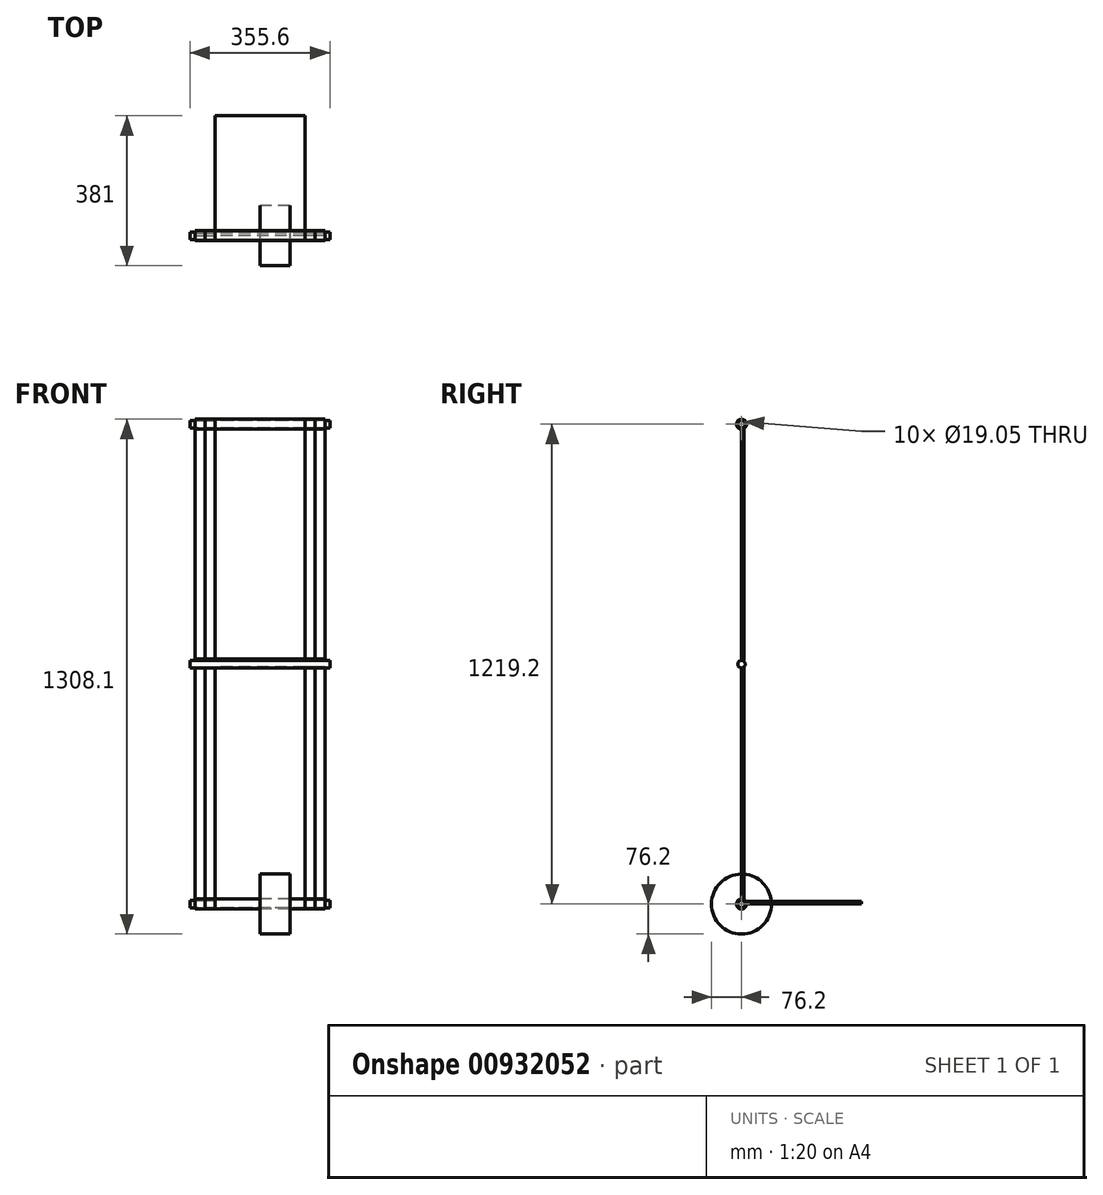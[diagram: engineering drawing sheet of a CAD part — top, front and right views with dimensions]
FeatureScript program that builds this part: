
annotation { "Feature Type Name" : "Feature", "Feature Type Description" : "" }
export const myFeature = defineFeature(function(context is Context, id is Id, definition is map)
    precondition{}
    {
        {
            var Q0;
            Q0=qCreatedBy(makeId("Right.planeOp"),FACE);
            var sketch = newSketch(context, id + "F0", { "sketchPlane" : qUnion([Q0])});
            skLineSegment(sketch, "E0", {"start": v(0, 0) * mm, "end": v(0, 1219.2) * mm});
            skLineSegment(sketch, "E1", {"start": v(0, 0) * mm, "end": v(304.8, 0) * mm});
            skLineSegment(sketch, "E2.0", {"start": v(6.35, 6.35) * mm, "end": v(6.35, 1219.2) * mm});
            skLineSegment(sketch, "E3.0", {"start": v(6.35, 6.35) * mm, "end": v(304.8, 6.35) * mm});
            skLineSegment(sketch, "E4", {"start": v(304.8, 6.35) * mm, "end": v(304.8, 0) * mm});
            skLineSegment(sketch, "E5", {"start": v(0, 1219.2) * mm, "end": v(6.35, 1219.2) * mm});
            skCircle(sketch, "E6", {"center": v(0, 0) * mm, "radius": 12.7 * mm});
            skCircle(sketch, "E7", {"center": v(0, 609.6) * mm, "radius": 12.7 * mm});
            skCircle(sketch, "E8", {"center": v(0, 1219.2) * mm, "radius": 12.7 * mm});
            skCircle(sketch, "E9", {"center": v(0, 609.6) * mm, "radius": 9.53 * mm});
            skCircle(sketch, "E10", {"center": v(0, 1219.2) * mm, "radius": 9.53 * mm});
            skCircle(sketch, "E11", {"center": v(0, 0) * mm, "radius": 9.53 * mm});
            skSolve(sketch);
        }
        {
            var Q0;
            {var subQ0=sQuery(id+"F0.wireOp",EDGE,"E7");var subQ1=sQuery(id+"F0.wireOp",EDGE,"E0");var subQ2=makeQuery(id+"F0.imprint","INTERSECT",VERTEX,{"disambiguationData":[OD(0.0)],"derivedFrom":[subQ1,subQ0]});Q0=makeQuery(id+"F0.imprint","IMPRINT",FACE,{"disambiguationData":[TD([[makeQuery(id+"F0.imprint","IMPRINT",EDGE,{"disambiguationData":[TD([[subQ2,-1.0]])],"derivedFrom":subQ1}),1.0]])]});}
            var Q1;
            {var subQ0=sQuery(id+"F0.wireOp",EDGE,"E4");Q1=makeQuery(id+"F0.imprint","IMPRINT",FACE,{"disambiguationData":[TD([[makeQuery(id+"F0.imprint","IMPRINT",EDGE,{"derivedFrom":subQ0}),-1.0]])]});}
            var Q2;
            {var subQ0=sQuery(id+"F0.wireOp",EDGE,"E7");var subQ1=sQuery(id+"F0.wireOp",EDGE,"E2.0");var subQ2=makeQuery(id+"F0.imprint","INTERSECT",VERTEX,{"disambiguationData":[OD(0.0)],"derivedFrom":[subQ1,subQ0]});Q2=makeQuery(id+"F0.imprint","IMPRINT",FACE,{"disambiguationData":[TD([[makeQuery(id+"F0.imprint","IMPRINT",EDGE,{"disambiguationData":[TD([[subQ2,-1.0]])],"derivedFrom":subQ1}),-1.0]])]});}
            var Q3;
            {var subQ0=sQuery(id+"F0.wireOp",EDGE,"E8");var subQ1=sQuery(id+"F0.wireOp",EDGE,"E0");var subQ2=makeQuery(id+"F0.imprint","INTERSECT",VERTEX,{"derivedFrom":[subQ1,subQ0]});Q3=makeQuery(id+"F0.imprint","IMPRINT",FACE,{"disambiguationData":[TD([[makeQuery(id+"F0.imprint","IMPRINT",EDGE,{"disambiguationData":[TD([[subQ2,-1.0]])],"derivedFrom":subQ1}),1.0]])]});}
            var Q4;
            {var subQ0=sQuery(id+"F0.wireOp",EDGE,"E7");var subQ1=sQuery(id+"F0.wireOp",EDGE,"E0");var subQ2=makeQuery(id+"F0.imprint","INTERSECT",VERTEX,{"disambiguationData":[OD(0.0)],"derivedFrom":[subQ1,subQ0]});Q4=makeQuery(id+"F0.imprint","IMPRINT",FACE,{"disambiguationData":[TD([[makeQuery(id+"F0.imprint","IMPRINT",EDGE,{"disambiguationData":[TD([[subQ2,-1.0]])],"derivedFrom":subQ1}),-1.0]])]});}
            var Q5;
            {var subQ0=sQuery(id+"F0.wireOp",EDGE,"E6");var subQ1=sQuery(id+"F0.wireOp",EDGE,"E0");var subQ2=makeQuery(id+"F0.imprint","INTERSECT",VERTEX,{"derivedFrom":[subQ1,subQ0]});Q5=makeQuery(id+"F0.imprint","IMPRINT",FACE,{"disambiguationData":[TD([[makeQuery(id+"F0.imprint","IMPRINT",EDGE,{"disambiguationData":[TD([[subQ2,-1.0]])],"derivedFrom":subQ1}),-1.0]])]});}
            var Q6;
            {var subQ0=sQuery(id+"F0.wireOp",EDGE,"E8");var subQ1=sQuery(id+"F0.wireOp",EDGE,"E0");var subQ2=makeQuery(id+"F0.imprint","INTERSECT",VERTEX,{"derivedFrom":[subQ1,subQ0]});Q6=makeQuery(id+"F0.imprint","IMPRINT",FACE,{"disambiguationData":[TD([[makeQuery(id+"F0.imprint","IMPRINT",EDGE,{"disambiguationData":[TD([[subQ2,-1.0]])],"derivedFrom":subQ1}),-1.0]])]});}
            var Q7;
            {var subQ0=sQuery(id+"F0.wireOp",EDGE,"E7");var subQ1=sQuery(id+"F0.wireOp",EDGE,"E0");var subQ2=makeQuery(id+"F0.imprint","INTERSECT",VERTEX,{"disambiguationData":[OD(1.0)],"derivedFrom":[subQ1,subQ0]});Q7=makeQuery(id+"F0.imprint","IMPRINT",FACE,{"disambiguationData":[TD([[makeQuery(id+"F0.imprint","IMPRINT",EDGE,{"disambiguationData":[TD([[subQ2,-1.0]])],"derivedFrom":subQ1}),-1.0]])]});}
            var Q8;
            {var subQ0=sQuery(id+"F0.wireOp",EDGE,"E7");var subQ1=sQuery(id+"F0.wireOp",EDGE,"E0");var subQ2=makeQuery(id+"F0.imprint","INTERSECT",VERTEX,{"disambiguationData":[OD(1.0)],"derivedFrom":[subQ1,subQ0]});Q8=makeQuery(id+"F0.imprint","IMPRINT",FACE,{"disambiguationData":[TD([[makeQuery(id+"F0.imprint","IMPRINT",EDGE,{"disambiguationData":[TD([[subQ2,1.0]])],"derivedFrom":subQ1}),-1.0]])]});}
            var Q9;
            {var subQ0=sQuery(id+"F0.wireOp",EDGE,"E6");var subQ1=sQuery(id+"F0.wireOp",EDGE,"E0");var subQ2=makeQuery(id+"F0.imprint","INTERSECT",VERTEX,{"derivedFrom":[subQ1,subQ0]});Q9=makeQuery(id+"F0.imprint","IMPRINT",FACE,{"disambiguationData":[TD([[makeQuery(id+"F0.imprint","IMPRINT",EDGE,{"disambiguationData":[TD([[subQ2,1.0]])],"derivedFrom":subQ1}),-1.0]])]});}
            var Q10;
            {var subQ0=sQuery(id+"F0.wireOp",EDGE,"E6");var subQ1=sQuery(id+"F0.wireOp",EDGE,"E2.0");var subQ2=makeQuery(id+"F0.imprint","INTERSECT",VERTEX,{"derivedFrom":[subQ1,subQ0]});Q10=makeQuery(id+"F0.imprint","IMPRINT",FACE,{"disambiguationData":[TD([[makeQuery(id+"F0.imprint","IMPRINT",EDGE,{"disambiguationData":[TD([[subQ2,1.0]])],"derivedFrom":subQ1}),-1.0]])]});}
            var Q11;
            {var subQ0=sQuery(id+"F0.wireOp",EDGE,"E6");var subQ1=sQuery(id+"F0.wireOp",EDGE,"E1");var subQ2=makeQuery(id+"F0.imprint","INTERSECT",VERTEX,{"derivedFrom":[subQ1,subQ0]});Q11=makeQuery(id+"F0.imprint","IMPRINT",FACE,{"disambiguationData":[TD([[makeQuery(id+"F0.imprint","IMPRINT",EDGE,{"disambiguationData":[TD([[subQ2,1.0]])],"derivedFrom":subQ1}),1.0]])]});}
            var Q12;
            {var subQ0=sQuery(id+"F0.wireOp",EDGE,"E6");var subQ1=sQuery(id+"F0.wireOp",EDGE,"E0");var subQ2=makeQuery(id+"F0.imprint","INTERSECT",VERTEX,{"derivedFrom":[subQ1,subQ0]});Q12=makeQuery(id+"F0.imprint","IMPRINT",FACE,{"disambiguationData":[TD([[makeQuery(id+"F0.imprint","IMPRINT",EDGE,{"disambiguationData":[TD([[subQ2,1.0]])],"derivedFrom":subQ1}),1.0]])]});}
            extrude(context, id + "F1", {"entities" : qUnion([Q0, Q1, Q2, Q3, Q4, Q5, Q6, Q7, Q8, Q9, Q10, Q11, Q12]), "endBound" : BoundingType.SYMMETRIC, "depth" : 228.6 * mm, "offsetDistance" : 25.4 * mm});
        }
        {
            var Q0;
            {var subQ0=sQuery(id+"F0.wireOp",EDGE,"E7");var subQ1=sQuery(id+"F0.wireOp",EDGE,"E0");var subQ2=makeQuery(id+"F0.imprint","INTERSECT",VERTEX,{"disambiguationData":[OD(0.0)],"derivedFrom":[subQ1,subQ0]});Q0=makeQuery(id+"F0.imprint","IMPRINT",FACE,{"disambiguationData":[TD([[makeQuery(id+"F0.imprint","IMPRINT",EDGE,{"disambiguationData":[TD([[subQ2,-1.0]])],"derivedFrom":subQ1}),1.0]])]});}
            var Q1;
            {var subQ0=sQuery(id+"F0.wireOp",EDGE,"E6");var subQ1=sQuery(id+"F0.wireOp",EDGE,"E2.0");var subQ2=makeQuery(id+"F0.imprint","INTERSECT",VERTEX,{"derivedFrom":[subQ1,subQ0]});Q1=makeQuery(id+"F0.imprint","IMPRINT",FACE,{"disambiguationData":[TD([[makeQuery(id+"F0.imprint","IMPRINT",EDGE,{"disambiguationData":[TD([[subQ2,1.0]])],"derivedFrom":subQ1}),-1.0]])]});}
            var Q2;
            {var subQ0=sQuery(id+"F0.wireOp",EDGE,"E7");var subQ1=sQuery(id+"F0.wireOp",EDGE,"E2.0");var subQ2=makeQuery(id+"F0.imprint","INTERSECT",VERTEX,{"disambiguationData":[OD(0.0)],"derivedFrom":[subQ1,subQ0]});Q2=makeQuery(id+"F0.imprint","IMPRINT",FACE,{"disambiguationData":[TD([[makeQuery(id+"F0.imprint","IMPRINT",EDGE,{"disambiguationData":[TD([[subQ2,-1.0]])],"derivedFrom":subQ1}),-1.0]])]});}
            var Q3;
            {var subQ0=sQuery(id+"F0.wireOp",EDGE,"E8");var subQ1=sQuery(id+"F0.wireOp",EDGE,"E0");var subQ2=makeQuery(id+"F0.imprint","INTERSECT",VERTEX,{"derivedFrom":[subQ1,subQ0]});Q3=makeQuery(id+"F0.imprint","IMPRINT",FACE,{"disambiguationData":[TD([[makeQuery(id+"F0.imprint","IMPRINT",EDGE,{"disambiguationData":[TD([[subQ2,-1.0]])],"derivedFrom":subQ1}),1.0]])]});}
            var Q4;
            {var subQ0=sQuery(id+"F0.wireOp",EDGE,"E7");var subQ1=sQuery(id+"F0.wireOp",EDGE,"E0");var subQ2=makeQuery(id+"F0.imprint","INTERSECT",VERTEX,{"disambiguationData":[OD(1.0)],"derivedFrom":[subQ1,subQ0]});Q4=makeQuery(id+"F0.imprint","IMPRINT",FACE,{"disambiguationData":[TD([[makeQuery(id+"F0.imprint","IMPRINT",EDGE,{"disambiguationData":[TD([[subQ2,1.0]])],"derivedFrom":subQ1}),-1.0]])]});}
            var Q5;
            {var subQ0=sQuery(id+"F0.wireOp",EDGE,"E7");var subQ1=sQuery(id+"F0.wireOp",EDGE,"E0");var subQ2=makeQuery(id+"F0.imprint","INTERSECT",VERTEX,{"disambiguationData":[OD(0.0)],"derivedFrom":[subQ1,subQ0]});Q5=makeQuery(id+"F0.imprint","IMPRINT",FACE,{"disambiguationData":[TD([[makeQuery(id+"F0.imprint","IMPRINT",EDGE,{"disambiguationData":[TD([[subQ2,-1.0]])],"derivedFrom":subQ1}),-1.0]])]});}
            var Q6;
            {var subQ0=sQuery(id+"F0.wireOp",EDGE,"E6");var subQ1=sQuery(id+"F0.wireOp",EDGE,"E0");var subQ2=makeQuery(id+"F0.imprint","INTERSECT",VERTEX,{"derivedFrom":[subQ1,subQ0]});Q6=makeQuery(id+"F0.imprint","IMPRINT",FACE,{"disambiguationData":[TD([[makeQuery(id+"F0.imprint","IMPRINT",EDGE,{"disambiguationData":[TD([[subQ2,1.0]])],"derivedFrom":subQ1}),1.0]])]});}
            var Q7;
            {var subQ0=sQuery(id+"F0.wireOp",EDGE,"E6");var subQ1=sQuery(id+"F0.wireOp",EDGE,"E0");var subQ2=makeQuery(id+"F0.imprint","INTERSECT",VERTEX,{"derivedFrom":[subQ1,subQ0]});Q7=makeQuery(id+"F0.imprint","IMPRINT",FACE,{"disambiguationData":[TD([[makeQuery(id+"F0.imprint","IMPRINT",EDGE,{"disambiguationData":[TD([[subQ2,-1.0]])],"derivedFrom":subQ1}),-1.0]])]});}
            var Q8;
            {var subQ0=sQuery(id+"F0.wireOp",EDGE,"E7");var subQ1=sQuery(id+"F0.wireOp",EDGE,"E0");var subQ2=makeQuery(id+"F0.imprint","INTERSECT",VERTEX,{"disambiguationData":[OD(1.0)],"derivedFrom":[subQ1,subQ0]});Q8=makeQuery(id+"F0.imprint","IMPRINT",FACE,{"disambiguationData":[TD([[makeQuery(id+"F0.imprint","IMPRINT",EDGE,{"disambiguationData":[TD([[subQ2,-1.0]])],"derivedFrom":subQ1}),-1.0]])]});}
            var Q9;
            {var subQ0=sQuery(id+"F0.wireOp",EDGE,"E6");var subQ1=sQuery(id+"F0.wireOp",EDGE,"E0");var subQ2=makeQuery(id+"F0.imprint","INTERSECT",VERTEX,{"derivedFrom":[subQ1,subQ0]});Q9=makeQuery(id+"F0.imprint","IMPRINT",FACE,{"disambiguationData":[TD([[makeQuery(id+"F0.imprint","IMPRINT",EDGE,{"disambiguationData":[TD([[subQ2,1.0]])],"derivedFrom":subQ1}),-1.0]])]});}
            var Q10;
            {var subQ0=sQuery(id+"F0.wireOp",EDGE,"E8");var subQ1=sQuery(id+"F0.wireOp",EDGE,"E0");var subQ2=makeQuery(id+"F0.imprint","INTERSECT",VERTEX,{"derivedFrom":[subQ1,subQ0]});Q10=makeQuery(id+"F0.imprint","IMPRINT",FACE,{"disambiguationData":[TD([[makeQuery(id+"F0.imprint","IMPRINT",EDGE,{"disambiguationData":[TD([[subQ2,-1.0]])],"derivedFrom":subQ1}),-1.0]])]});}
            var Q11;
            {var subQ0=sQuery(id+"F0.wireOp",EDGE,"E6");var subQ1=sQuery(id+"F0.wireOp",EDGE,"E1");var subQ2=makeQuery(id+"F0.imprint","INTERSECT",VERTEX,{"derivedFrom":[subQ1,subQ0]});Q11=makeQuery(id+"F0.imprint","IMPRINT",FACE,{"disambiguationData":[TD([[makeQuery(id+"F0.imprint","IMPRINT",EDGE,{"disambiguationData":[TD([[subQ2,1.0]])],"derivedFrom":subQ1}),1.0]])]});}
            extrude(context, id + "F2", {"entities" : qUnion([Q0, Q1, Q2, Q3, Q4, Q5, Q6, Q7, Q8, Q9, Q10, Q11]), "depth" : 139.7 * mm, "offsetDistance" : 25.4 * mm, "hasSecondDirection" : true, "secondDirectionOppositeDirection" : false, "secondDirectionDepth" : 114.3 * mm});
        }
        {
            var Q0;
            {var subQ0=sQuery(id+"F0.wireOp",EDGE,"E6");var subQ1=sQuery(id+"F0.wireOp",EDGE,"E2.0");var subQ2=makeQuery(id+"F0.imprint","INTERSECT",VERTEX,{"derivedFrom":[subQ1,subQ0]});Q0=makeQuery(id+"F0.imprint","IMPRINT",FACE,{"disambiguationData":[TD([[makeQuery(id+"F0.imprint","IMPRINT",EDGE,{"disambiguationData":[TD([[subQ2,1.0]])],"derivedFrom":subQ1}),-1.0]])]});}
            var Q1;
            {var subQ0=sQuery(id+"F0.wireOp",EDGE,"E6");var subQ1=sQuery(id+"F0.wireOp",EDGE,"E0");var subQ2=makeQuery(id+"F0.imprint","INTERSECT",VERTEX,{"derivedFrom":[subQ1,subQ0]});Q1=makeQuery(id+"F0.imprint","IMPRINT",FACE,{"disambiguationData":[TD([[makeQuery(id+"F0.imprint","IMPRINT",EDGE,{"disambiguationData":[TD([[subQ2,1.0]])],"derivedFrom":subQ1}),-1.0]])]});}
            var Q2;
            {var subQ0=sQuery(id+"F0.wireOp",EDGE,"E7");var subQ1=sQuery(id+"F0.wireOp",EDGE,"E0");var subQ2=makeQuery(id+"F0.imprint","INTERSECT",VERTEX,{"disambiguationData":[OD(0.0)],"derivedFrom":[subQ1,subQ0]});Q2=makeQuery(id+"F0.imprint","IMPRINT",FACE,{"disambiguationData":[TD([[makeQuery(id+"F0.imprint","IMPRINT",EDGE,{"disambiguationData":[TD([[subQ2,-1.0]])],"derivedFrom":subQ1}),1.0]])]});}
            var Q3;
            {var subQ0=sQuery(id+"F0.wireOp",EDGE,"E8");var subQ1=sQuery(id+"F0.wireOp",EDGE,"E0");var subQ2=makeQuery(id+"F0.imprint","INTERSECT",VERTEX,{"derivedFrom":[subQ1,subQ0]});Q3=makeQuery(id+"F0.imprint","IMPRINT",FACE,{"disambiguationData":[TD([[makeQuery(id+"F0.imprint","IMPRINT",EDGE,{"disambiguationData":[TD([[subQ2,-1.0]])],"derivedFrom":subQ1}),1.0]])]});}
            var Q4;
            {var subQ0=sQuery(id+"F0.wireOp",EDGE,"E6");var subQ1=sQuery(id+"F0.wireOp",EDGE,"E0");var subQ2=makeQuery(id+"F0.imprint","INTERSECT",VERTEX,{"derivedFrom":[subQ1,subQ0]});Q4=makeQuery(id+"F0.imprint","IMPRINT",FACE,{"disambiguationData":[TD([[makeQuery(id+"F0.imprint","IMPRINT",EDGE,{"disambiguationData":[TD([[subQ2,-1.0]])],"derivedFrom":subQ1}),-1.0]])]});}
            var Q5;
            {var subQ0=sQuery(id+"F0.wireOp",EDGE,"E7");var subQ1=sQuery(id+"F0.wireOp",EDGE,"E0");var subQ2=makeQuery(id+"F0.imprint","INTERSECT",VERTEX,{"disambiguationData":[OD(1.0)],"derivedFrom":[subQ1,subQ0]});Q5=makeQuery(id+"F0.imprint","IMPRINT",FACE,{"disambiguationData":[TD([[makeQuery(id+"F0.imprint","IMPRINT",EDGE,{"disambiguationData":[TD([[subQ2,1.0]])],"derivedFrom":subQ1}),-1.0]])]});}
            var Q6;
            {var subQ0=sQuery(id+"F0.wireOp",EDGE,"E7");var subQ1=sQuery(id+"F0.wireOp",EDGE,"E0");var subQ2=makeQuery(id+"F0.imprint","INTERSECT",VERTEX,{"disambiguationData":[OD(1.0)],"derivedFrom":[subQ1,subQ0]});Q6=makeQuery(id+"F0.imprint","IMPRINT",FACE,{"disambiguationData":[TD([[makeQuery(id+"F0.imprint","IMPRINT",EDGE,{"disambiguationData":[TD([[subQ2,-1.0]])],"derivedFrom":subQ1}),-1.0]])]});}
            var Q7;
            {var subQ0=sQuery(id+"F0.wireOp",EDGE,"E8");var subQ1=sQuery(id+"F0.wireOp",EDGE,"E0");var subQ2=makeQuery(id+"F0.imprint","INTERSECT",VERTEX,{"derivedFrom":[subQ1,subQ0]});Q7=makeQuery(id+"F0.imprint","IMPRINT",FACE,{"disambiguationData":[TD([[makeQuery(id+"F0.imprint","IMPRINT",EDGE,{"disambiguationData":[TD([[subQ2,-1.0]])],"derivedFrom":subQ1}),-1.0]])]});}
            var Q8;
            {var subQ0=sQuery(id+"F0.wireOp",EDGE,"E7");var subQ1=sQuery(id+"F0.wireOp",EDGE,"E0");var subQ2=makeQuery(id+"F0.imprint","INTERSECT",VERTEX,{"disambiguationData":[OD(0.0)],"derivedFrom":[subQ1,subQ0]});Q8=makeQuery(id+"F0.imprint","IMPRINT",FACE,{"disambiguationData":[TD([[makeQuery(id+"F0.imprint","IMPRINT",EDGE,{"disambiguationData":[TD([[subQ2,-1.0]])],"derivedFrom":subQ1}),-1.0]])]});}
            var Q9;
            {var subQ0=sQuery(id+"F0.wireOp",EDGE,"E7");var subQ1=sQuery(id+"F0.wireOp",EDGE,"E2.0");var subQ2=makeQuery(id+"F0.imprint","INTERSECT",VERTEX,{"disambiguationData":[OD(0.0)],"derivedFrom":[subQ1,subQ0]});Q9=makeQuery(id+"F0.imprint","IMPRINT",FACE,{"disambiguationData":[TD([[makeQuery(id+"F0.imprint","IMPRINT",EDGE,{"disambiguationData":[TD([[subQ2,-1.0]])],"derivedFrom":subQ1}),-1.0]])]});}
            var Q10;
            {var subQ0=sQuery(id+"F0.wireOp",EDGE,"E6");var subQ1=sQuery(id+"F0.wireOp",EDGE,"E1");var subQ2=makeQuery(id+"F0.imprint","INTERSECT",VERTEX,{"derivedFrom":[subQ1,subQ0]});Q10=makeQuery(id+"F0.imprint","IMPRINT",FACE,{"disambiguationData":[TD([[makeQuery(id+"F0.imprint","IMPRINT",EDGE,{"disambiguationData":[TD([[subQ2,1.0]])],"derivedFrom":subQ1}),1.0]])]});}
            var Q11;
            {var subQ0=sQuery(id+"F0.wireOp",EDGE,"E6");var subQ1=sQuery(id+"F0.wireOp",EDGE,"E0");var subQ2=makeQuery(id+"F0.imprint","INTERSECT",VERTEX,{"derivedFrom":[subQ1,subQ0]});Q11=makeQuery(id+"F0.imprint","IMPRINT",FACE,{"disambiguationData":[TD([[makeQuery(id+"F0.imprint","IMPRINT",EDGE,{"disambiguationData":[TD([[subQ2,1.0]])],"derivedFrom":subQ1}),1.0]])]});}
            extrude(context, id + "F3", {"entities" : qUnion([Q0, Q1, Q2, Q3, Q4, Q5, Q6, Q7, Q8, Q9, Q10, Q11]), "oppositeDirection" : true, "depth" : 139.7 * mm, "offsetDistance" : 25.4 * mm, "hasSecondDirection" : true, "secondDirectionOppositeDirection" : true, "secondDirectionDepth" : 114.3 * mm});
        }
        {
            var Q0;
            {var subQ0=sQuery(id+"F0.wireOp",EDGE,"E8");var subQ1=sQuery(id+"F0.wireOp",EDGE,"E0");var subQ2=makeQuery(id+"F0.imprint","INTERSECT",VERTEX,{"derivedFrom":[subQ1,subQ0]});Q0=makeQuery(id+"F0.imprint","IMPRINT",FACE,{"disambiguationData":[TD([[makeQuery(id+"F0.imprint","IMPRINT",EDGE,{"disambiguationData":[TD([[subQ2,-1.0]])],"derivedFrom":subQ1}),-1.0]])]});}
            var Q1;
            {var subQ0=sQuery(id+"F0.wireOp",EDGE,"E6");var subQ1=sQuery(id+"F0.wireOp",EDGE,"E0");var subQ2=makeQuery(id+"F0.imprint","INTERSECT",VERTEX,{"derivedFrom":[subQ1,subQ0]});Q1=makeQuery(id+"F0.imprint","IMPRINT",FACE,{"disambiguationData":[TD([[makeQuery(id+"F0.imprint","IMPRINT",EDGE,{"disambiguationData":[TD([[subQ2,1.0]])],"derivedFrom":subQ1}),-1.0]])]});}
            var Q2;
            {var subQ0=sQuery(id+"F0.wireOp",EDGE,"E7");var subQ1=sQuery(id+"F0.wireOp",EDGE,"E0");var subQ2=makeQuery(id+"F0.imprint","INTERSECT",VERTEX,{"disambiguationData":[OD(0.0)],"derivedFrom":[subQ1,subQ0]});Q2=makeQuery(id+"F0.imprint","IMPRINT",FACE,{"disambiguationData":[TD([[makeQuery(id+"F0.imprint","IMPRINT",EDGE,{"disambiguationData":[TD([[subQ2,-1.0]])],"derivedFrom":subQ1}),-1.0]])]});}
            var Q3;
            {var subQ0=sQuery(id+"F0.wireOp",EDGE,"E7");var subQ1=sQuery(id+"F0.wireOp",EDGE,"E2.0");var subQ2=makeQuery(id+"F0.imprint","INTERSECT",VERTEX,{"disambiguationData":[OD(0.0)],"derivedFrom":[subQ1,subQ0]});Q3=makeQuery(id+"F0.imprint","IMPRINT",FACE,{"disambiguationData":[TD([[makeQuery(id+"F0.imprint","IMPRINT",EDGE,{"disambiguationData":[TD([[subQ2,-1.0]])],"derivedFrom":subQ1}),-1.0]])]});}
            var Q4;
            {var subQ0=sQuery(id+"F0.wireOp",EDGE,"E7");var subQ1=sQuery(id+"F0.wireOp",EDGE,"E0");var subQ2=makeQuery(id+"F0.imprint","INTERSECT",VERTEX,{"disambiguationData":[OD(1.0)],"derivedFrom":[subQ1,subQ0]});Q4=makeQuery(id+"F0.imprint","IMPRINT",FACE,{"disambiguationData":[TD([[makeQuery(id+"F0.imprint","IMPRINT",EDGE,{"disambiguationData":[TD([[subQ2,1.0]])],"derivedFrom":subQ1}),-1.0]])]});}
            var Q5;
            {var subQ0=sQuery(id+"F0.wireOp",EDGE,"E7");var subQ1=sQuery(id+"F0.wireOp",EDGE,"E0");var subQ2=makeQuery(id+"F0.imprint","INTERSECT",VERTEX,{"disambiguationData":[OD(0.0)],"derivedFrom":[subQ1,subQ0]});Q5=makeQuery(id+"F0.imprint","IMPRINT",FACE,{"disambiguationData":[TD([[makeQuery(id+"F0.imprint","IMPRINT",EDGE,{"disambiguationData":[TD([[subQ2,-1.0]])],"derivedFrom":subQ1}),1.0]])]});}
            var Q6;
            {var subQ0=sQuery(id+"F0.wireOp",EDGE,"E6");var subQ1=sQuery(id+"F0.wireOp",EDGE,"E0");var subQ2=makeQuery(id+"F0.imprint","INTERSECT",VERTEX,{"derivedFrom":[subQ1,subQ0]});Q6=makeQuery(id+"F0.imprint","IMPRINT",FACE,{"disambiguationData":[TD([[makeQuery(id+"F0.imprint","IMPRINT",EDGE,{"disambiguationData":[TD([[subQ2,-1.0]])],"derivedFrom":subQ1}),-1.0]])]});}
            var Q7;
            {var subQ0=sQuery(id+"F0.wireOp",EDGE,"E7");var subQ1=sQuery(id+"F0.wireOp",EDGE,"E0");var subQ2=makeQuery(id+"F0.imprint","INTERSECT",VERTEX,{"disambiguationData":[OD(1.0)],"derivedFrom":[subQ1,subQ0]});Q7=makeQuery(id+"F0.imprint","IMPRINT",FACE,{"disambiguationData":[TD([[makeQuery(id+"F0.imprint","IMPRINT",EDGE,{"disambiguationData":[TD([[subQ2,-1.0]])],"derivedFrom":subQ1}),-1.0]])]});}
            var Q8;
            {var subQ0=sQuery(id+"F0.wireOp",EDGE,"E6");var subQ1=sQuery(id+"F0.wireOp",EDGE,"E2.0");var subQ2=makeQuery(id+"F0.imprint","INTERSECT",VERTEX,{"derivedFrom":[subQ1,subQ0]});Q8=makeQuery(id+"F0.imprint","IMPRINT",FACE,{"disambiguationData":[TD([[makeQuery(id+"F0.imprint","IMPRINT",EDGE,{"disambiguationData":[TD([[subQ2,1.0]])],"derivedFrom":subQ1}),-1.0]])]});}
            var Q9;
            {var subQ0=sQuery(id+"F0.wireOp",EDGE,"E8");var subQ1=sQuery(id+"F0.wireOp",EDGE,"E0");var subQ2=makeQuery(id+"F0.imprint","INTERSECT",VERTEX,{"derivedFrom":[subQ1,subQ0]});Q9=makeQuery(id+"F0.imprint","IMPRINT",FACE,{"disambiguationData":[TD([[makeQuery(id+"F0.imprint","IMPRINT",EDGE,{"disambiguationData":[TD([[subQ2,-1.0]])],"derivedFrom":subQ1}),1.0]])]});}
            var Q10;
            {var subQ0=sQuery(id+"F0.wireOp",EDGE,"E6");var subQ1=sQuery(id+"F0.wireOp",EDGE,"E1");var subQ2=makeQuery(id+"F0.imprint","INTERSECT",VERTEX,{"derivedFrom":[subQ1,subQ0]});Q10=makeQuery(id+"F0.imprint","IMPRINT",FACE,{"disambiguationData":[TD([[makeQuery(id+"F0.imprint","IMPRINT",EDGE,{"disambiguationData":[TD([[subQ2,1.0]])],"derivedFrom":subQ1}),1.0]])]});}
            var Q11;
            {var subQ0=sQuery(id+"F0.wireOp",EDGE,"E6");var subQ1=sQuery(id+"F0.wireOp",EDGE,"E0");var subQ2=makeQuery(id+"F0.imprint","INTERSECT",VERTEX,{"derivedFrom":[subQ1,subQ0]});Q11=makeQuery(id+"F0.imprint","IMPRINT",FACE,{"disambiguationData":[TD([[makeQuery(id+"F0.imprint","IMPRINT",EDGE,{"disambiguationData":[TD([[subQ2,1.0]])],"derivedFrom":subQ1}),1.0]])]});}
            extrude(context, id + "F4", {"entities" : qUnion([Q0, Q1, Q2, Q3, Q4, Q5, Q6, Q7, Q8, Q9, Q10, Q11]), "depth" : 165.1 * mm, "offsetDistance" : 25.4 * mm, "hasSecondDirection" : true, "secondDirectionOppositeDirection" : false, "secondDirectionDepth" : 139.7 * mm});
        }
        {
            var Q0;
            {var subQ0=sQuery(id+"F0.wireOp",EDGE,"E6");var subQ1=sQuery(id+"F0.wireOp",EDGE,"E0");var subQ2=makeQuery(id+"F0.imprint","INTERSECT",VERTEX,{"derivedFrom":[subQ1,subQ0]});Q0=makeQuery(id+"F0.imprint","IMPRINT",FACE,{"disambiguationData":[TD([[makeQuery(id+"F0.imprint","IMPRINT",EDGE,{"disambiguationData":[TD([[subQ2,1.0]])],"derivedFrom":subQ1}),-1.0]])]});}
            var Q1;
            {var subQ0=sQuery(id+"F0.wireOp",EDGE,"E6");var subQ1=sQuery(id+"F0.wireOp",EDGE,"E0");var subQ2=makeQuery(id+"F0.imprint","INTERSECT",VERTEX,{"derivedFrom":[subQ1,subQ0]});Q1=makeQuery(id+"F0.imprint","IMPRINT",FACE,{"disambiguationData":[TD([[makeQuery(id+"F0.imprint","IMPRINT",EDGE,{"disambiguationData":[TD([[subQ2,1.0]])],"derivedFrom":subQ1}),1.0]])]});}
            var Q2;
            {var subQ0=sQuery(id+"F0.wireOp",EDGE,"E6");var subQ1=sQuery(id+"F0.wireOp",EDGE,"E2.0");var subQ2=makeQuery(id+"F0.imprint","INTERSECT",VERTEX,{"derivedFrom":[subQ1,subQ0]});Q2=makeQuery(id+"F0.imprint","IMPRINT",FACE,{"disambiguationData":[TD([[makeQuery(id+"F0.imprint","IMPRINT",EDGE,{"disambiguationData":[TD([[subQ2,1.0]])],"derivedFrom":subQ1}),-1.0]])]});}
            var Q3;
            {var subQ0=sQuery(id+"F0.wireOp",EDGE,"E6");var subQ1=sQuery(id+"F0.wireOp",EDGE,"E0");var subQ2=makeQuery(id+"F0.imprint","INTERSECT",VERTEX,{"derivedFrom":[subQ1,subQ0]});Q3=makeQuery(id+"F0.imprint","IMPRINT",FACE,{"disambiguationData":[TD([[makeQuery(id+"F0.imprint","IMPRINT",EDGE,{"disambiguationData":[TD([[subQ2,-1.0]])],"derivedFrom":subQ1}),-1.0]])]});}
            var Q4;
            {var subQ0=sQuery(id+"F0.wireOp",EDGE,"E7");var subQ1=sQuery(id+"F0.wireOp",EDGE,"E0");var subQ2=makeQuery(id+"F0.imprint","INTERSECT",VERTEX,{"disambiguationData":[OD(1.0)],"derivedFrom":[subQ1,subQ0]});Q4=makeQuery(id+"F0.imprint","IMPRINT",FACE,{"disambiguationData":[TD([[makeQuery(id+"F0.imprint","IMPRINT",EDGE,{"disambiguationData":[TD([[subQ2,1.0]])],"derivedFrom":subQ1}),-1.0]])]});}
            var Q5;
            {var subQ0=sQuery(id+"F0.wireOp",EDGE,"E6");var subQ1=sQuery(id+"F0.wireOp",EDGE,"E1");var subQ2=makeQuery(id+"F0.imprint","INTERSECT",VERTEX,{"derivedFrom":[subQ1,subQ0]});Q5=makeQuery(id+"F0.imprint","IMPRINT",FACE,{"disambiguationData":[TD([[makeQuery(id+"F0.imprint","IMPRINT",EDGE,{"disambiguationData":[TD([[subQ2,1.0]])],"derivedFrom":subQ1}),1.0]])]});}
            var Q6;
            {var subQ0=sQuery(id+"F0.wireOp",EDGE,"E7");var subQ1=sQuery(id+"F0.wireOp",EDGE,"E0");var subQ2=makeQuery(id+"F0.imprint","INTERSECT",VERTEX,{"disambiguationData":[OD(0.0)],"derivedFrom":[subQ1,subQ0]});Q6=makeQuery(id+"F0.imprint","IMPRINT",FACE,{"disambiguationData":[TD([[makeQuery(id+"F0.imprint","IMPRINT",EDGE,{"disambiguationData":[TD([[subQ2,-1.0]])],"derivedFrom":subQ1}),-1.0]])]});}
            var Q7;
            {var subQ0=sQuery(id+"F0.wireOp",EDGE,"E7");var subQ1=sQuery(id+"F0.wireOp",EDGE,"E0");var subQ2=makeQuery(id+"F0.imprint","INTERSECT",VERTEX,{"disambiguationData":[OD(0.0)],"derivedFrom":[subQ1,subQ0]});Q7=makeQuery(id+"F0.imprint","IMPRINT",FACE,{"disambiguationData":[TD([[makeQuery(id+"F0.imprint","IMPRINT",EDGE,{"disambiguationData":[TD([[subQ2,-1.0]])],"derivedFrom":subQ1}),1.0]])]});}
            var Q8;
            {var subQ0=sQuery(id+"F0.wireOp",EDGE,"E8");var subQ1=sQuery(id+"F0.wireOp",EDGE,"E0");var subQ2=makeQuery(id+"F0.imprint","INTERSECT",VERTEX,{"derivedFrom":[subQ1,subQ0]});Q8=makeQuery(id+"F0.imprint","IMPRINT",FACE,{"disambiguationData":[TD([[makeQuery(id+"F0.imprint","IMPRINT",EDGE,{"disambiguationData":[TD([[subQ2,-1.0]])],"derivedFrom":subQ1}),-1.0]])]});}
            var Q9;
            {var subQ0=sQuery(id+"F0.wireOp",EDGE,"E7");var subQ1=sQuery(id+"F0.wireOp",EDGE,"E0");var subQ2=makeQuery(id+"F0.imprint","INTERSECT",VERTEX,{"disambiguationData":[OD(1.0)],"derivedFrom":[subQ1,subQ0]});Q9=makeQuery(id+"F0.imprint","IMPRINT",FACE,{"disambiguationData":[TD([[makeQuery(id+"F0.imprint","IMPRINT",EDGE,{"disambiguationData":[TD([[subQ2,-1.0]])],"derivedFrom":subQ1}),-1.0]])]});}
            var Q10;
            {var subQ0=sQuery(id+"F0.wireOp",EDGE,"E8");var subQ1=sQuery(id+"F0.wireOp",EDGE,"E0");var subQ2=makeQuery(id+"F0.imprint","INTERSECT",VERTEX,{"derivedFrom":[subQ1,subQ0]});Q10=makeQuery(id+"F0.imprint","IMPRINT",FACE,{"disambiguationData":[TD([[makeQuery(id+"F0.imprint","IMPRINT",EDGE,{"disambiguationData":[TD([[subQ2,-1.0]])],"derivedFrom":subQ1}),1.0]])]});}
            var Q11;
            {var subQ0=sQuery(id+"F0.wireOp",EDGE,"E7");var subQ1=sQuery(id+"F0.wireOp",EDGE,"E2.0");var subQ2=makeQuery(id+"F0.imprint","INTERSECT",VERTEX,{"disambiguationData":[OD(0.0)],"derivedFrom":[subQ1,subQ0]});Q11=makeQuery(id+"F0.imprint","IMPRINT",FACE,{"disambiguationData":[TD([[makeQuery(id+"F0.imprint","IMPRINT",EDGE,{"disambiguationData":[TD([[subQ2,-1.0]])],"derivedFrom":subQ1}),-1.0]])]});}
            extrude(context, id + "F5", {"entities" : qUnion([Q0, Q1, Q2, Q3, Q4, Q5, Q6, Q7, Q8, Q9, Q10, Q11]), "oppositeDirection" : true, "depth" : 165.1 * mm, "offsetDistance" : 25.4 * mm, "hasSecondDirection" : true, "secondDirectionOppositeDirection" : true, "secondDirectionDepth" : 139.7 * mm});
        }
        {
            var Q0;
            {var subQ0=sQuery(id+"F0.wireOp",EDGE,"E9");var subQ1=sQuery(id+"F0.wireOp",EDGE,"E0");var subQ2=makeQuery(id+"F0.imprint","INTERSECT",VERTEX,{"disambiguationData":[OD(0.0)],"derivedFrom":[subQ1,subQ0]});Q0=makeQuery(id+"F0.imprint","IMPRINT",FACE,{"disambiguationData":[TD([[makeQuery(id+"F0.imprint","IMPRINT",EDGE,{"disambiguationData":[TD([[subQ2,-1.0]])],"derivedFrom":subQ1}),1.0]])]});}
            var Q1;
            {var subQ0=sQuery(id+"F0.wireOp",EDGE,"E5");Q1=makeQuery(id+"F0.imprint","IMPRINT",FACE,{"disambiguationData":[TD([[makeQuery(id+"F0.imprint","IMPRINT",EDGE,{"derivedFrom":subQ0}),-1.0]])]});}
            var Q2;
            {var subQ0=sQuery(id+"F0.wireOp",EDGE,"E1");var subQ1=sQuery(id+"F0.wireOp",EDGE,"E0");var subQ2=makeQuery(id+"F0.imprint","INTERSECT",VERTEX,{"derivedFrom":[subQ1,subQ0]});Q2=makeQuery(id+"F0.imprint","IMPRINT",FACE,{"disambiguationData":[TD([[makeQuery(id+"F0.imprint","IMPRINT",EDGE,{"disambiguationData":[TD([[subQ2,-1.0]])],"derivedFrom":subQ1}),1.0]])]});}
            var Q3;
            {var subQ6=sQuery(id+"F0.wireOp",EDGE,"E1");var subQ7=sQuery(id+"F0.wireOp",EDGE,"E0");var subQ8=makeQuery(id+"F0.imprint","INTERSECT",VERTEX,{"derivedFrom":[subQ7,subQ6]});Q3=makeQuery(id+"F0.imprint","IMPRINT",FACE,{"disambiguationData":[TD([[makeQuery(id+"F0.imprint","IMPRINT",EDGE,{"disambiguationData":[TD([[subQ8,-1.0]])],"derivedFrom":subQ7}),-1.0]])]});}
            var Q4;
            {var subQ0=sQuery(id+"F0.wireOp",EDGE,"E9");var subQ1=sQuery(id+"F0.wireOp",EDGE,"E0");var subQ2=makeQuery(id+"F0.imprint","INTERSECT",VERTEX,{"disambiguationData":[OD(0.0)],"derivedFrom":[subQ1,subQ0]});Q4=makeQuery(id+"F0.imprint","IMPRINT",FACE,{"disambiguationData":[TD([[makeQuery(id+"F0.imprint","IMPRINT",EDGE,{"disambiguationData":[TD([[subQ2,-1.0]])],"derivedFrom":subQ1}),-1.0]])]});}
            var Q5;
            {var subQ0=sQuery(id+"F0.wireOp",EDGE,"E9");var subQ1=sQuery(id+"F0.wireOp",EDGE,"E2.0");var subQ2=makeQuery(id+"F0.imprint","INTERSECT",VERTEX,{"disambiguationData":[OD(0.0)],"derivedFrom":[subQ1,subQ0]});Q5=makeQuery(id+"F0.imprint","IMPRINT",FACE,{"disambiguationData":[TD([[makeQuery(id+"F0.imprint","IMPRINT",EDGE,{"disambiguationData":[TD([[subQ2,-1.0]])],"derivedFrom":subQ1}),-1.0]])]});}
            var Q6;
            {var subQ0=sQuery(id+"F0.wireOp",EDGE,"E5");Q6=makeQuery(id+"F0.imprint","IMPRINT",FACE,{"disambiguationData":[TD([[makeQuery(id+"F0.imprint","IMPRINT",EDGE,{"derivedFrom":subQ0}),1.0]])]});}
            var Q7;
            {var subQ0=sQuery(id+"F0.wireOp",EDGE,"E3.0");var subQ1=sQuery(id+"F0.wireOp",EDGE,"E2.0");var subQ2=makeQuery(id+"F0.imprint","INTERSECT",VERTEX,{"derivedFrom":[subQ1,subQ0]});Q7=makeQuery(id+"F0.imprint","IMPRINT",FACE,{"disambiguationData":[TD([[makeQuery(id+"F0.imprint","IMPRINT",EDGE,{"disambiguationData":[TD([[subQ2,-1.0]])],"derivedFrom":subQ1}),-1.0]])]});}
            extrude(context, id + "F6", {"entities" : qUnion([Q0, Q1, Q2, Q3, Q4, Q5, Q6, Q7]), "endBound" : BoundingType.SYMMETRIC, "depth" : 355.6 * mm, "offsetDistance" : 25.4 * mm});
        }
        {
            var Q0;
            Q0=qCreatedBy(makeId("Right.planeOp"),FACE);
            var sketch = newSketch(context, id + "F7", { "sketchPlane" : qUnion([Q0])});
            skCircle(sketch, "E12", {"center": v(0, 0) * mm, "radius": 76.2 * mm});
            skSolve(sketch);
        }
        {
            var Q0;
            Q0=makeQuery(id+"F7.imprint","IMPRINT",FACE,{"disambiguationData":[TD([[makeQuery(id+"F7.imprint","IMPRINT",EDGE,{"derivedFrom":sQuery(id+"F7.wireOp",EDGE,"E12")}),1.0]])]});
            extrude(context, id + "F8", {"entities" : qUnion([Q0]), "depth" : 76.2 * mm, "offsetDistance" : 25.4 * mm});
        }
    });
